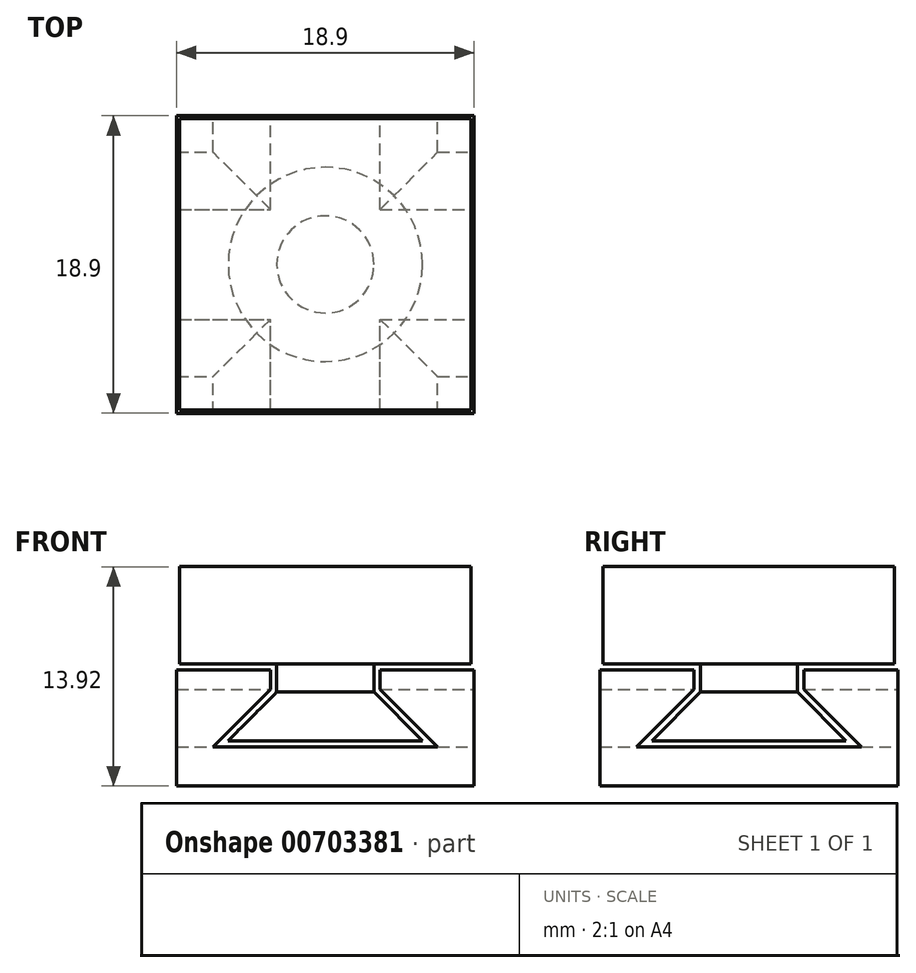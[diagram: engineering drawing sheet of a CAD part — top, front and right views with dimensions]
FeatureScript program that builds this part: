
annotation { "Feature Type Name" : "Feature", "Feature Type Description" : "" }
export const myFeature = defineFeature(function(context is Context, id is Id, definition is map)
    precondition{}
    {
        {
            assignVariable(context, id + "F0", {"name" : "tollerance", "anyValue" : 0.4});
        }
        {
            assignVariable(context, id + "F1", {"name" : "Base", "anyValue" : 19});
        }
        {
            assignVariable(context, id + "F2", {"name" : "scale", "anyValue" : getVariable(context, 'Base') / (15 + getVariable(context, 'tollerance'))});
        }
        {
            var Q0;
            Q0=qCreatedBy(makeId("Front.planeOp"),FACE);
            var sketch = newSketch(context, id + "F3", { "sketchPlane" : qUnion([Q0])});
            skLineSegment(sketch, "E0", {"start": v(0, 4.88) * mm, "end": v(-9.25, 4.88) * mm});
            skLineSegment(sketch, "E1", {"start": v(-9.25, 4.88) * mm, "end": v(-9.25, 11.05) * mm});
            skLineSegment(sketch, "E2", {"start": v(-9.25, 11.05) * mm, "end": v(0, 11.05) * mm});
            skLineSegment(sketch, "E3", {"start": v(0, 11.05) * mm, "end": v(0, 4.88) * mm});
            skLineSegment(sketch, "E4", {"start": v(-3.08, 4.88) * mm, "end": v(-3.08, 3.08) * mm});
            skLineSegment(sketch, "E5", {"start": v(-3.08, 3.08) * mm, "end": v(-6.17, 0) * mm});
            skLineSegment(sketch, "E6", {"start": v(-6.17, 0) * mm, "end": v(0, 0) * mm});
            skLineSegment(sketch, "E7", {"start": v(0, 0) * mm, "end": v(0, 4.88) * mm});
            skLineSegment(sketch, "E8.0", {"start": v(-3.48, 3.25) * mm, "end": v(-6.73, 0) * mm});
            skLineSegment(sketch, "E8.1", {"start": v(-3.48, 4.48) * mm, "end": v(-3.48, 3.25) * mm});
            skLineSegment(sketch, "E9.0", {"start": v(-3.48, 4.48) * mm, "end": v(-9.25, 4.48) * mm});
            skLineSegment(sketch, "E10", {"start": v(-9.25, 4.88) * mm, "end": v(-9.25, 0) * mm, "construction": true});
            skLineSegment(sketch, "E11.bottom", {"start": v(0, 11.05) * mm, "end": v(9.25, 11.05) * mm});
            skLineSegment(sketch, "E11.top", {"start": v(0, 4.88) * mm, "end": v(9.25, 4.88) * mm});
            skLineSegment(sketch, "E11.right", {"start": v(9.25, 11.05) * mm, "end": v(9.25, 4.88) * mm});
            skSolve(sketch);
        }
        {
            var Q0;
            {var subQ0=sQuery(id+"F3.wireOp",EDGE,"E1");Q0=makeQuery(id+"F3.imprint","IMPRINT",FACE,{"disambiguationData":[TD([[makeQuery(id+"F3.imprint","IMPRINT",EDGE,{"derivedFrom":subQ0}),-1.0]])]});}
            var Q1;
            Q1=makeQuery(id+"F3.imprint","IMPRINT",FACE,{"disambiguationData":[TD([[makeQuery(id+"F3.imprint","IMPRINT",EDGE,{"derivedFrom":sQuery(id+"F3.wireOp",EDGE,"E11.bottom")}),-1.0]])]});
            extrude(context, id + "F4", {"entities" : qUnion([Q0, Q1]), "endBound" : BoundingType.SYMMETRIC, "depth" : (15 * getVariable(context, 'scale')) * mm, "offsetDistance" : 25 * mm});
        }
        {
            var Q0;
            {var subQ0=sQuery(id+"F3.wireOp",EDGE,"E4");Q0=makeQuery(id+"F3.imprint","IMPRINT",FACE,{"disambiguationData":[TD([[makeQuery(id+"F3.imprint","IMPRINT",EDGE,{"derivedFrom":subQ0}),1.0]])]});}
            var Q1;
            Q1=sQuery(id+"F3.wireOp",EDGE,"E7");
            revolve(context, id + "F5", {"operationType" : NewBodyOperationType.ADD, "surfaceOperationType" : NewSurfaceOperationType.NEW, "entities" : qUnion([Q0]), "axis" : qUnion([Q1]), "revolveType" : RevolveType.FULL});
        }
        {
            var Q0;
            Q0=qCreatedBy(makeId("Front.planeOp"),FACE);
            var sketch = newSketch(context, id + "F6", { "sketchPlane" : qUnion([Q0])});
            skLineSegment(sketch, "E12", {"start": v(-3.48, 4.48) * mm, "end": v(-3.48, 3.25) * mm});
            skLineSegment(sketch, "E13", {"start": v(-3.48, 3.25) * mm, "end": v(-7.13, -0.4) * mm});
            skLineSegment(sketch, "E14", {"start": v(-3.48, 4.48) * mm, "end": v(0, 4.48) * mm});
            skLineSegment(sketch, "E15", {"start": v(0, 4.48) * mm, "end": v(0, -0.4) * mm});
            skLineSegment(sketch, "E16", {"start": v(0, -0.4) * mm, "end": v(-7.13, -0.4) * mm});
            skLineSegment(sketch, "E17.MirrorCS", {"start": v(0, -0.4) * mm, "end": v(7.13, -0.4) * mm});
            skLineSegment(sketch, "E18.MirrorCS", {"start": v(3.48, 3.25) * mm, "end": v(7.13, -0.4) * mm});
            skLineSegment(sketch, "E19.MirrorCS", {"start": v(3.48, 4.48) * mm, "end": v(3.48, 3.25) * mm});
            skLineSegment(sketch, "E20.MirrorCS", {"start": v(3.48, 4.48) * mm, "end": v(0, 4.48) * mm});
            skLineSegment(sketch, "E21", {"start": v(-9.45, 4.48) * mm, "end": v(0, 4.48) * mm});
            skLineSegment(sketch, "E22", {"start": v(0, 4.48) * mm, "end": v(9.45, 4.48) * mm});
            skLineSegment(sketch, "E23", {"start": v(9.45, 4.48) * mm, "end": v(9.45, -2.87) * mm});
            skLineSegment(sketch, "E24", {"start": v(9.45, -2.87) * mm, "end": v(-9.45, -2.87) * mm});
            skLineSegment(sketch, "E25", {"start": v(-9.45, -2.87) * mm, "end": v(-9.45, 4.48) * mm});
            skLineSegment(sketch, "E26", {"start": v(-9.45, 4.88) * mm, "end": v(-9.25, 4.88) * mm, "construction": true});
            skLineSegment(sketch, "E27", {"start": v(9.45, 4.88) * mm, "end": v(9.25, 4.88) * mm, "construction": true});
            skLineSegment(sketch, "E28", {"start": v(0, 11.05) * mm, "end": v(-0.2, 11.05) * mm, "construction": true});
            skLineSegment(sketch, "E29", {"start": v(0, 11.05) * mm, "end": v(0.2, 11.05) * mm, "construction": true});
            skLineSegment(sketch, "E30", {"start": v(-0.2, 4.88) * mm, "end": v(0.2, 4.88) * mm, "construction": true});
            skSolve(sketch);
        }
        {
            var Q0;
            {var subQ4=sQuery(id+"F6.wireOp",EDGE,"E12");Q0=makeQuery(id+"F6.imprint","IMPRINT",FACE,{"disambiguationData":[TD([[makeQuery(id+"F6.imprint","IMPRINT",EDGE,{"derivedFrom":subQ4}),-1.0]])]});}
            var Q1;
            {var subQ1=sQuery(id+"F6.wireOp",EDGE,"E15");Q1=makeQuery(id+"F6.imprint","IMPRINT",FACE,{"disambiguationData":[TD([[makeQuery(id+"F6.imprint","IMPRINT",EDGE,{"derivedFrom":subQ1}),1.0]])]});}
            var Q2;
            {var subQ1=sQuery(id+"F6.wireOp",EDGE,"E12");Q2=makeQuery(id+"F6.imprint","IMPRINT",FACE,{"disambiguationData":[TD([[makeQuery(id+"F6.imprint","IMPRINT",EDGE,{"derivedFrom":subQ1}),1.0]])]});}
            extrude(context, id + "F7", {"entities" : qUnion([Q0, Q1, Q2]), "endBound" : BoundingType.SYMMETRIC, "depth" : ((15 * getVariable(context, 'scale')) + getVariable(context, 'tollerance')) * mm, "offsetDistance" : 25 * mm});
        }
        {
            var Q0;
            {var subQ1=sQuery(id+"F6.wireOp",EDGE,"E12");Q0=makeQuery(id+"F6.imprint","IMPRINT",FACE,{"disambiguationData":[TD([[makeQuery(id+"F6.imprint","IMPRINT",EDGE,{"derivedFrom":subQ1}),1.0]])]});}
            var Q1;
            {var subQ1=sQuery(id+"F6.wireOp",EDGE,"E15");Q1=makeQuery(id+"F6.imprint","IMPRINT",FACE,{"disambiguationData":[TD([[makeQuery(id+"F6.imprint","IMPRINT",EDGE,{"derivedFrom":subQ1}),1.0]])]});}
            extrude(context, id + "F8", {"entities" : qUnion([Q0, Q1]), "endBound" : BoundingType.SYMMETRIC, "depth" : (20 * getVariable(context, 'scale')) * mm, "offsetDistance" : 25 * mm});
        }
        {
            var Q0;
            Q0=makeQuery(id+"F8.opExtrude","SWEPT_BODY",BODY,{"disambiguationData":[OSD([sQuery(id+"F6.wireOp",EDGE,"E12"),sQuery(id+"F6.wireOp",EDGE,"E13"),sQuery(id+"F6.wireOp",EDGE,"E16"),sQuery(id+"F6.wireOp",EDGE,"E17.MirrorCS"),sQuery(id+"F6.wireOp",EDGE,"E18.MirrorCS"),sQuery(id+"F6.wireOp",EDGE,"E19.MirrorCS"),sQuery(id+"F6.wireOp",EDGE,"E21"),sQuery(id+"F6.wireOp",EDGE,"E22")])]});
            var Q1;
            Q1=makeQuery(id+"F7.opExtrude","SWEPT_BODY",BODY,{"disambiguationData":[OSD([sQuery(id+"F6.wireOp",EDGE,"E21"),sQuery(id+"F6.wireOp",EDGE,"E22"),sQuery(id+"F6.wireOp",EDGE,"E23"),sQuery(id+"F6.wireOp",EDGE,"E24"),sQuery(id+"F6.wireOp",EDGE,"E25")])]});
            booleanBodies(context, id + "F9", {"operationType" : BooleanOperationType.SUBTRACTION, "tools" : qUnion([Q0]), "targets" : qUnion([Q1]), "keepTools" : true});
        }
        {
            var Q0;
            Q0=makeQuery(id+"F8.opExtrude","SWEPT_BODY",BODY,{"disambiguationData":[OSD([sQuery(id+"F6.wireOp",EDGE,"E12"),sQuery(id+"F6.wireOp",EDGE,"E13"),sQuery(id+"F6.wireOp",EDGE,"E16"),sQuery(id+"F6.wireOp",EDGE,"E17.MirrorCS"),sQuery(id+"F6.wireOp",EDGE,"E18.MirrorCS"),sQuery(id+"F6.wireOp",EDGE,"E19.MirrorCS"),sQuery(id+"F6.wireOp",EDGE,"E21"),sQuery(id+"F6.wireOp",EDGE,"E22")])]});
            var Q1;
            Q1=sQuery(id+"F6.wireOp",EDGE,"E15");
            transform(context, id + "F10", {"entities" : qUnion([Q0]), "transformType" : TransformType.ROTATION, "transformAxis" : qUnion([Q1]), "angle" : 90 * degree, "makeCopy" : false});
        }
        {
            var Q0;
            Q0=makeQuery(id+"F8.opExtrude","SWEPT_BODY",BODY,{"disambiguationData":[OSD([sQuery(id+"F6.wireOp",EDGE,"E12"),sQuery(id+"F6.wireOp",EDGE,"E13"),sQuery(id+"F6.wireOp",EDGE,"E16"),sQuery(id+"F6.wireOp",EDGE,"E17.MirrorCS"),sQuery(id+"F6.wireOp",EDGE,"E18.MirrorCS"),sQuery(id+"F6.wireOp",EDGE,"E19.MirrorCS"),sQuery(id+"F6.wireOp",EDGE,"E21"),sQuery(id+"F6.wireOp",EDGE,"E22")])]});
            var Q1;
            Q1=makeQuery(id+"F7.opExtrude","SWEPT_BODY",BODY,{"disambiguationData":[OSD([sQuery(id+"F6.wireOp",EDGE,"E21"),sQuery(id+"F6.wireOp",EDGE,"E22"),sQuery(id+"F6.wireOp",EDGE,"E23"),sQuery(id+"F6.wireOp",EDGE,"E24"),sQuery(id+"F6.wireOp",EDGE,"E25")])]});
            booleanBodies(context, id + "F11", {"operationType" : BooleanOperationType.SUBTRACTION, "tools" : qUnion([Q0]), "targets" : qUnion([Q1])});
        }
    });
